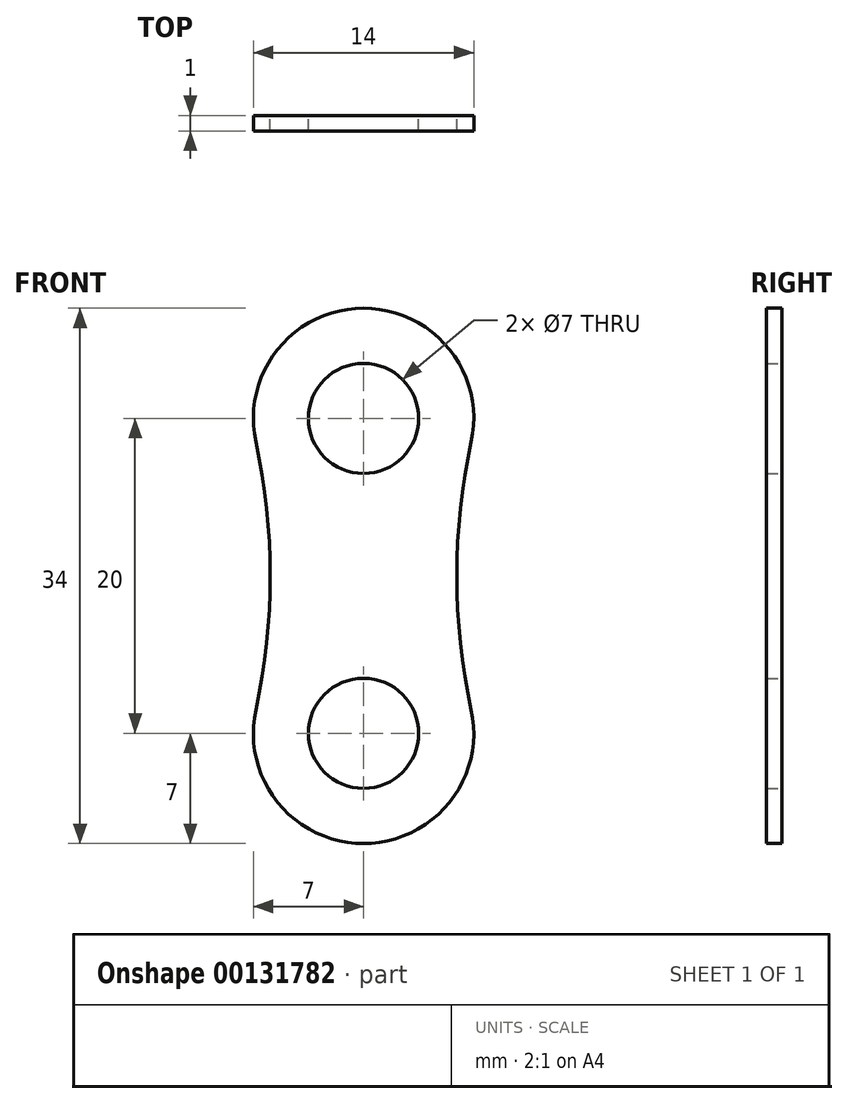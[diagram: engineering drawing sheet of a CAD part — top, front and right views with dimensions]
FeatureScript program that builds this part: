
annotation { "Feature Type Name" : "Feature", "Feature Type Description" : "" }
export const myFeature = defineFeature(function(context is Context, id is Id, definition is map)
    precondition{}
    {
        {
            var Q0;
            Q0=qCreatedBy(makeId("Front.planeOp"),FACE);
            var sketch = newSketch(context, id + "F0", { "sketchPlane" : qUnion([Q0])});
            skArc(sketch, "E0", {"start": v(6.84, -1.49) * mm, "mid": v(0, 7) * mm, "end": v(-6.84, -1.49) * mm});
            skArc(sketch, "E1", {"start": v(-6.84, -18.51) * mm, "mid": v(0, -27) * mm, "end": v(6.84, -18.51) * mm});
            skArc(sketch, "E2", {"start": v(-6.84, -18.51) * mm, "mid": v(-5.92, -10) * mm, "end": v(-6.84, -1.49) * mm});
            skArc(sketch, "E3", {"start": v(6.84, -1.49) * mm, "mid": v(5.92, -10) * mm, "end": v(6.84, -18.51) * mm});
            skCircle(sketch, "E4", {"center": v(0, 0) * mm, "radius": 3.5 * mm});
            skCircle(sketch, "E5", {"center": v(0, -20) * mm, "radius": 3.5 * mm});
            skSolve(sketch);
        }
        {
            var Q0;
            Q0=makeQuery(id+"F0.imprint","IMPRINT",FACE,{"disambiguationData":[TD([[makeQuery(id+"F0.imprint","IMPRINT",EDGE,{"derivedFrom":sQuery(id+"F0.wireOp",EDGE,"E0")}),1.0]])]});
            extrude(context, id + "F1", {"entities" : qUnion([Q0]), "depth" : 1 * mm});
        }
    });
